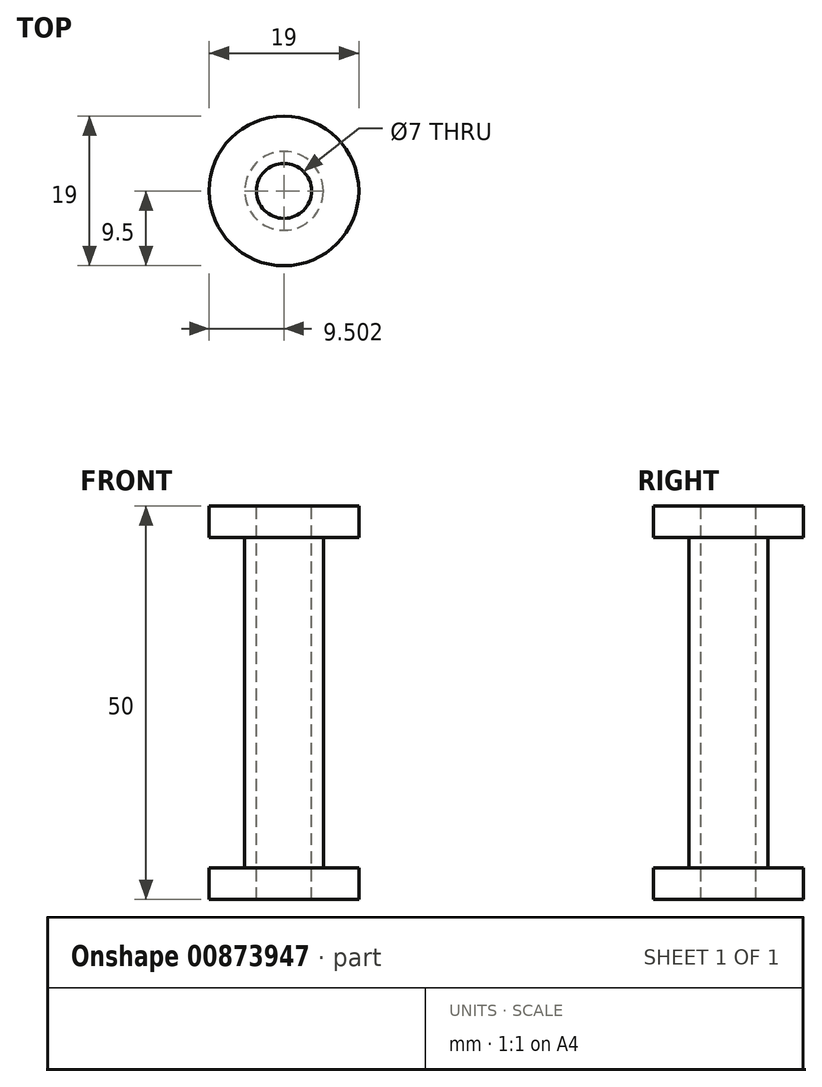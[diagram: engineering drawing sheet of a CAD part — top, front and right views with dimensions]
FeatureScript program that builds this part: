
annotation { "Feature Type Name" : "Feature", "Feature Type Description" : "" }
export const myFeature = defineFeature(function(context is Context, id is Id, definition is map)
    precondition{}
    {
        {
            var Q0;
            Q0=qCreatedBy(makeId("Front.planeOp"),FACE);
            var sketch = newSketch(context, id + "F0", { "sketchPlane" : qUnion([Q0])});
            skLineSegment(sketch, "E0.bottom", {"start": v(-4.78, -14.18) * mm, "end": v(14.22, -14.18) * mm});
            skLineSegment(sketch, "E0.top", {"start": v(-4.78, -18.18) * mm, "end": v(14.22, -18.18) * mm});
            skLineSegment(sketch, "E0.left", {"start": v(-4.78, -14.18) * mm, "end": v(-4.78, -18.18) * mm});
            skLineSegment(sketch, "E0.right", {"start": v(14.22, -14.18) * mm, "end": v(14.22, -18.18) * mm});
            skLineSegment(sketch, "E1.bottom", {"start": v(-0.28, -60.18) * mm, "end": v(9.72, -60.18) * mm});
            skLineSegment(sketch, "E1.top", {"start": v(-0.28, -18.18) * mm, "end": v(9.72, -18.18) * mm});
            skLineSegment(sketch, "E1.left", {"start": v(-0.28, -60.18) * mm, "end": v(-0.28, -18.18) * mm});
            skLineSegment(sketch, "E1.right", {"start": v(9.72, -60.18) * mm, "end": v(9.72, -18.18) * mm});
            skLineSegment(sketch, "E2.bottom", {"start": v(-4.78, -64.18) * mm, "end": v(14.22, -64.18) * mm});
            skLineSegment(sketch, "E2.top", {"start": v(-4.78, -60.18) * mm, "end": v(14.22, -60.18) * mm});
            skLineSegment(sketch, "E2.left", {"start": v(-4.78, -64.18) * mm, "end": v(-4.78, -60.18) * mm});
            skLineSegment(sketch, "E2.right", {"start": v(14.22, -64.18) * mm, "end": v(14.22, -60.18) * mm});
            skLineSegment(sketch, "E3", {"start": v(4.72, -5.05) * mm, "end": v(4.72, -71.93) * mm});
            skSolve(sketch);
        }
        {
            var Q0;
            {var subQ7=sQuery(id+"F0.wireOp",EDGE,"E0.right");Q0=makeQuery(id+"F0.imprint","IMPRINT",FACE,{"disambiguationData":[TD([[makeQuery(id+"F0.imprint","IMPRINT",EDGE,{"derivedFrom":subQ7}),-1.0]])]});}
            var Q1;
            {var subQ0=sQuery(id+"F0.wireOp",EDGE,"E1.right");Q1=makeQuery(id+"F0.imprint","IMPRINT",FACE,{"disambiguationData":[TD([[makeQuery(id+"F0.imprint","IMPRINT",EDGE,{"derivedFrom":subQ0}),1.0]])]});}
            var Q2;
            {var subQ0=sQuery(id+"F0.wireOp",EDGE,"E2.right");Q2=makeQuery(id+"F0.imprint","IMPRINT",FACE,{"disambiguationData":[TD([[makeQuery(id+"F0.imprint","IMPRINT",EDGE,{"derivedFrom":subQ0}),1.0]])]});}
            var Q3;
            Q3=sQuery(id+"F0.wireOp",EDGE,"E3");
            revolve(context, id + "F1", {"surfaceOperationType" : NewSurfaceOperationType.NEW, "entities" : qUnion([Q0, Q1, Q2]), "axis" : qUnion([Q3]), "revolveType" : RevolveType.FULL});
        }
        {
            var Q0;
            Q0=qCreatedBy(makeId("Top.planeOp"),FACE);
            var sketch = newSketch(context, id + "F2", { "sketchPlane" : qUnion([Q0])});
            skCircle(sketch, "E4", {"center": v(4.72, 0) * mm, "radius": 3.5 * mm});
            skSolve(sketch);
        }
        {
            var Q0;
            Q0=makeQuery(id+"F2.imprint","IMPRINT",FACE,{"disambiguationData":[TD([[makeQuery(id+"F2.imprint","IMPRINT",EDGE,{"derivedFrom":sQuery(id+"F2.wireOp",EDGE,"E4")}),1.0]])]});
            extrude(context, id + "F3", {"entities" : qUnion([Q0]), "operationType" : NewBodyOperationType.REMOVE, "oppositeDirection" : true, "depth" : 71 * mm, "offsetDistance" : 25 * mm});
        }
    });
